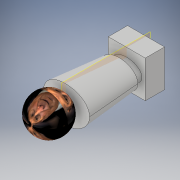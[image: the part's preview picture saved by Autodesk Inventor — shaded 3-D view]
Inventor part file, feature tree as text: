
AUTODESK INVENTOR PART (.ipt)
format: ipt  version: 2017 (Build 210142000, 142)  size: 259,584 bytes
history: native  units: in
note: dims shown in document units (in); Inventor stores cm internally (conversion verified against a paired STEP export)
features: sketch x5, extrude x4, projected_geometry x3, plane x1, revolve x1
ambient origin geometry x8: Origin, YZ Plane, XZ Plane, XY Plane, X Axis, Y Axis, Z Axis, Center Point
bodies: Solid1 (feature_tree)
feature tree (14):
  extrude  "Extrusion1"  Depth=0.575in
  extrude  "Extrusion2"  Depth=0.236in
  extrude  "Extrusion3"  Depth=0.115in TaperAngle=0.0deg
  plane  "Work Plane1"
  extrude  "Extrusion4"  Depth=0.84in
  revolve  "Revolution2"  Angle=90.0deg
  sketch  "Sketch1"  dims[d0=0.575in d1=0.575in]
  sketch  "Sketch2"  dims[d2=0.3in d3=0.0in d4=0.236in]
  sketch  "Sketch3"  dims[d5=0.155in d6=0.115in d7=0.0in]
  sketch  "Sketch4"  dims[d8=0.05in d9=0.84in d10=0.0344in]
  projected_geometry  "Projected Loop1"
  projected_geometry  "Projected Loop2"
  sketch  "Sketch6"  dims[d12=0.84in d13=0.0in d18=90.0deg]
  projected_geometry  "Projected Loop4"
